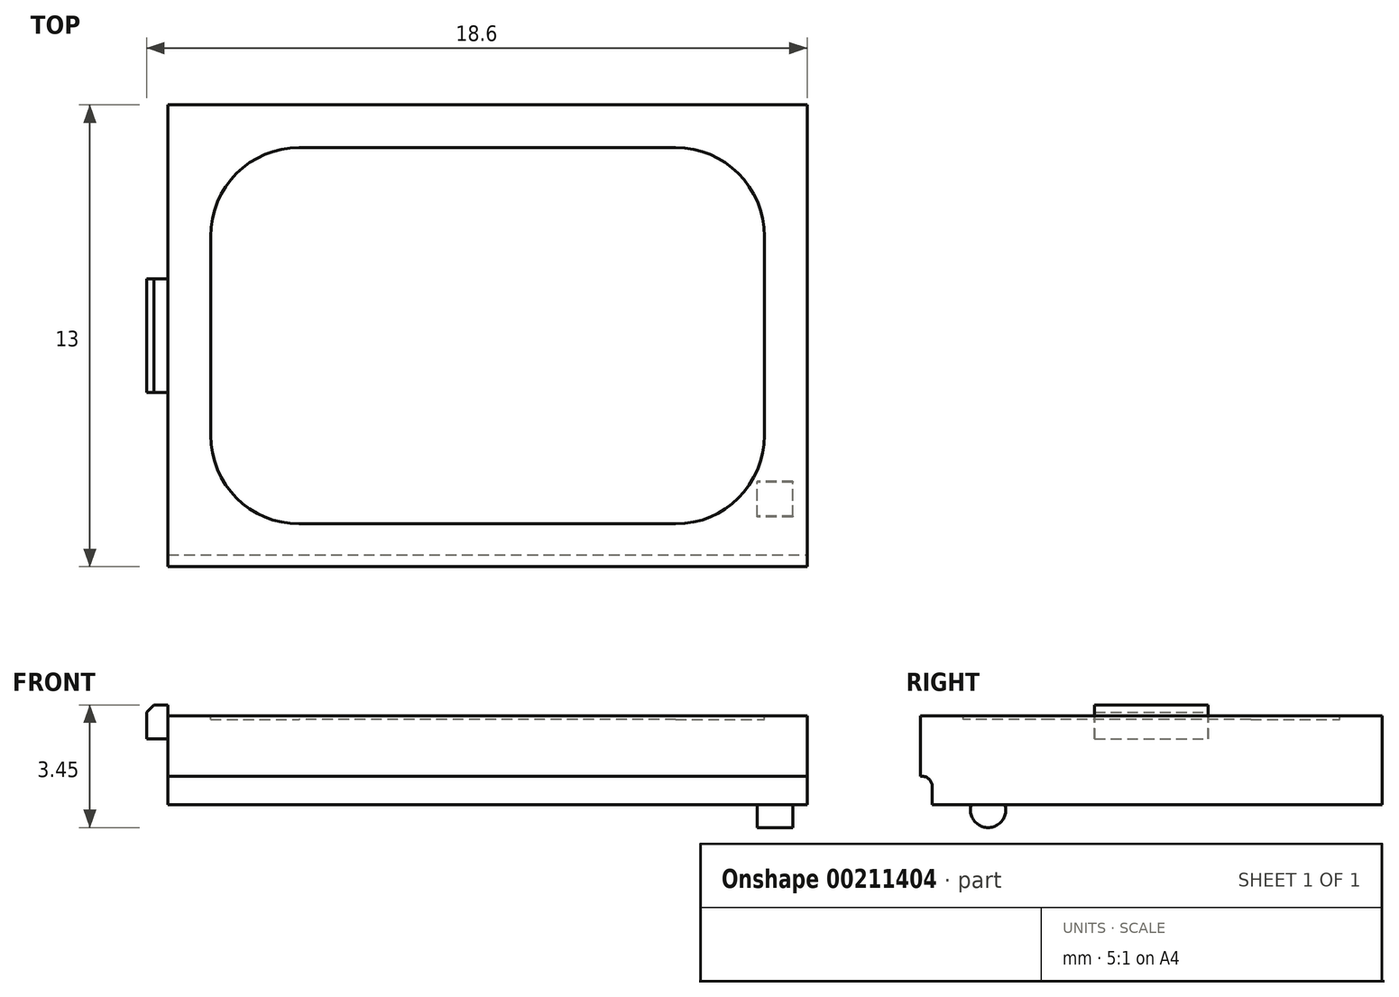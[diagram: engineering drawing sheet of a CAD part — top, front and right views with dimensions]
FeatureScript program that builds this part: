
annotation { "Feature Type Name" : "Feature", "Feature Type Description" : "" }
export const myFeature = defineFeature(function(context is Context, id is Id, definition is map)
    precondition{}
    {
        {
            var Q0;
            Q0=qCreatedBy(makeId("Top.planeOp"),FACE);
            var sketch = newSketch(context, id + "F0", { "sketchPlane" : qUnion([Q0])});
            skLineSegment(sketch, "E0.bottom", {"start": v(9, 6.5) * mm, "end": v(-9, 6.5) * mm});
            skLineSegment(sketch, "E0.top", {"start": v(9, -6.5) * mm, "end": v(-9, -6.5) * mm});
            skLineSegment(sketch, "E0.left", {"start": v(9, 6.5) * mm, "end": v(9, -6.5) * mm});
            skLineSegment(sketch, "E0.right", {"start": v(-9, 6.5) * mm, "end": v(-9, -6.5) * mm});
            skPoint(sketch, "E0.middle", {"position": v(0, 0) * mm});
            skSolve(sketch);
        }
        {
            var Q0;
            Q0=qSketchRegion(id+"F0",true);
            extrude(context, id + "F1", {"entities" : qUnion([Q0]), "depth" : 2.5 * mm});
        }
        {
            var Q0;
            Q0=makeQuery(id+"F1.opExtrude","CAP_FACE",FACE,{"disambiguationData":[OSD([sQuery(id+"F0.wireOp",EDGE,"E0.bottom"),sQuery(id+"F0.wireOp",EDGE,"E0.top"),sQuery(id+"F0.wireOp",EDGE,"E0.left"),sQuery(id+"F0.wireOp",EDGE,"E0.right")])],"isStart":false});
            var sketch = newSketch(context, id + "F2", { "sketchPlane" : qUnion([Q0])});
            skLineSegment(sketch, "E1.bottom", {"start": v(5.3, 5.3) * mm, "end": v(-5.3, 5.3) * mm});
            skLineSegment(sketch, "E1.top", {"start": v(5.3, -5.3) * mm, "end": v(-5.3, -5.3) * mm});
            skLineSegment(sketch, "E1.left", {"start": v(7.8, 2.8) * mm, "end": v(7.8, -2.8) * mm});
            skLineSegment(sketch, "E1.right", {"start": v(-7.8, 2.8) * mm, "end": v(-7.8, -2.8) * mm});
            skPoint(sketch, "E1.middle", {"position": v(0, 0) * mm});
            skPoint(sketch, "E2.visualSharp", {"position": v(-7.8, 5.3) * mm});
            skArc(sketch, "E2.filletArc", {"start": v(-5.3, 5.3) * mm, "mid": v(-7.07, 4.57) * mm, "end": v(-7.8, 2.8) * mm});
            skPoint(sketch, "E3.visualSharp", {"position": v(-7.8, -5.3) * mm});
            skArc(sketch, "E3.filletArc", {"start": v(-7.8, -2.8) * mm, "mid": v(-7.07, -4.57) * mm, "end": v(-5.3, -5.3) * mm});
            skPoint(sketch, "E4.visualSharp", {"position": v(7.8, -5.3) * mm});
            skArc(sketch, "E4.filletArc", {"start": v(5.3, -5.3) * mm, "mid": v(7.07, -4.57) * mm, "end": v(7.8, -2.8) * mm});
            skPoint(sketch, "E5.visualSharp", {"position": v(7.8, 5.3) * mm});
            skArc(sketch, "E5.filletArc", {"start": v(7.8, 2.8) * mm, "mid": v(7.07, 4.57) * mm, "end": v(5.3, 5.3) * mm});
            skSolve(sketch);
        }
        {
            var Q0;
            Q0=qSketchRegion(id+"F2",true);
            extrude(context, id + "F3", {"entities" : qUnion([Q0]), "operationType" : NewBodyOperationType.REMOVE, "oppositeDirection" : true, "depth" : .1 * mm});
        }
        {
            var Q0;
            Q0=qCreatedBy(makeId("Right.planeOp"),FACE);
            cPlane(context, id + "F4", {"entities" : qUnion([Q0]), "cplaneType" : CPlaneType.OFFSET, "offset" : 8.1 * mm, "width" : 150 * mm, "height" : 150 * mm});
        }
        {
            var Q0;
            Q0=qCreatedBy(id+"F4.planeOp",FACE);
            var sketch = newSketch(context, id + "F5", { "sketchPlane" : qUnion([Q0])});
            skCircle(sketch, "E6", {"center": v(-4.6, -0.15) * mm, "radius": 0.5 * mm});
            skLineSegment(sketch, "E7", {"start": v(-4.6, -0.15) * mm, "end": v(-4.6, -0.65) * mm, "construction": true});
            skSolve(sketch);
        }
        {
            var Q0;
            Q0=qSketchRegion(id+"F5",true);
            extrude(context, id + "F6", {"entities" : qUnion([Q0]), "operationType" : NewBodyOperationType.ADD, "endBound" : BoundingType.SYMMETRIC, "depth" : 1 * mm});
        }
        {
            var Q0;
            Q0=qCreatedBy(makeId("Right.planeOp"),FACE);
            var sketch = newSketch(context, id + "F7", { "sketchPlane" : qUnion([Q0])});
            skLineSegment(sketch, "E8.bottom", {"start": v(-6.5, 0) * mm, "end": v(-6.18, 0) * mm});
            skLineSegment(sketch, "E8.top", {"start": v(-6.5, 0.8) * mm, "end": v(-6.48, 0.8) * mm});
            skLineSegment(sketch, "E8.left", {"start": v(-6.5, 0) * mm, "end": v(-6.5, 0.8) * mm});
            skLineSegment(sketch, "E8.right", {"start": v(-6.18, 0) * mm, "end": v(-6.18, 0.5) * mm});
            skPoint(sketch, "E9.visualSharp", {"position": v(-6.18, 0.8) * mm});
            skArc(sketch, "E9.filletArc", {"start": v(-6.18, 0.5) * mm, "mid": v(-6.26, 0.71) * mm, "end": v(-6.48, 0.8) * mm});
            skSolve(sketch);
        }
        {
            var Q0;
            Q0=qSketchRegion(id+"F7",true);
            extrude(context, id + "F8", {"entities" : qUnion([Q0]), "operationType" : NewBodyOperationType.REMOVE, "endBound" : BoundingType.THROUGH_ALL, "oppositeDirection" : true, "depth" : 25 * mm, "hasSecondDirection" : true, "secondDirectionBound" : SecondDirectionBoundingType.THROUGH_ALL, "secondDirectionOppositeDirection" : false, "secondDirectionDepth" : 25 * mm});
        }
        {
            var Q0;
            Q0=qCreatedBy(makeId("Front.planeOp"),FACE);
            var sketch = newSketch(context, id + "F9", { "sketchPlane" : qUnion([Q0])});
            skLineSegment(sketch, "E10", {"start": v(-9, 2.8) * mm, "end": v(-9.4, 2.8) * mm});
            skLineSegment(sketch, "E11", {"start": v(-9.4, 2.8) * mm, "end": v(-9.6, 2.6) * mm});
            skLineSegment(sketch, "E12", {"start": v(-9.6, 2.6) * mm, "end": v(-9.6, 1.85) * mm});
            skLineSegment(sketch, "E13", {"start": v(-9.6, 1.85) * mm, "end": v(-9, 1.85) * mm});
            skLineSegment(sketch, "E14", {"start": v(-9, 1.85) * mm, "end": v(-9, 2.8) * mm});
            skSolve(sketch);
        }
        {
            var Q0;
            Q0=qSketchRegion(id+"F9",true);
            extrude(context, id + "F10", {"entities" : qUnion([Q0]), "operationType" : NewBodyOperationType.ADD, "endBound" : BoundingType.SYMMETRIC, "depth" : 3.2 * mm});
        }
    });
